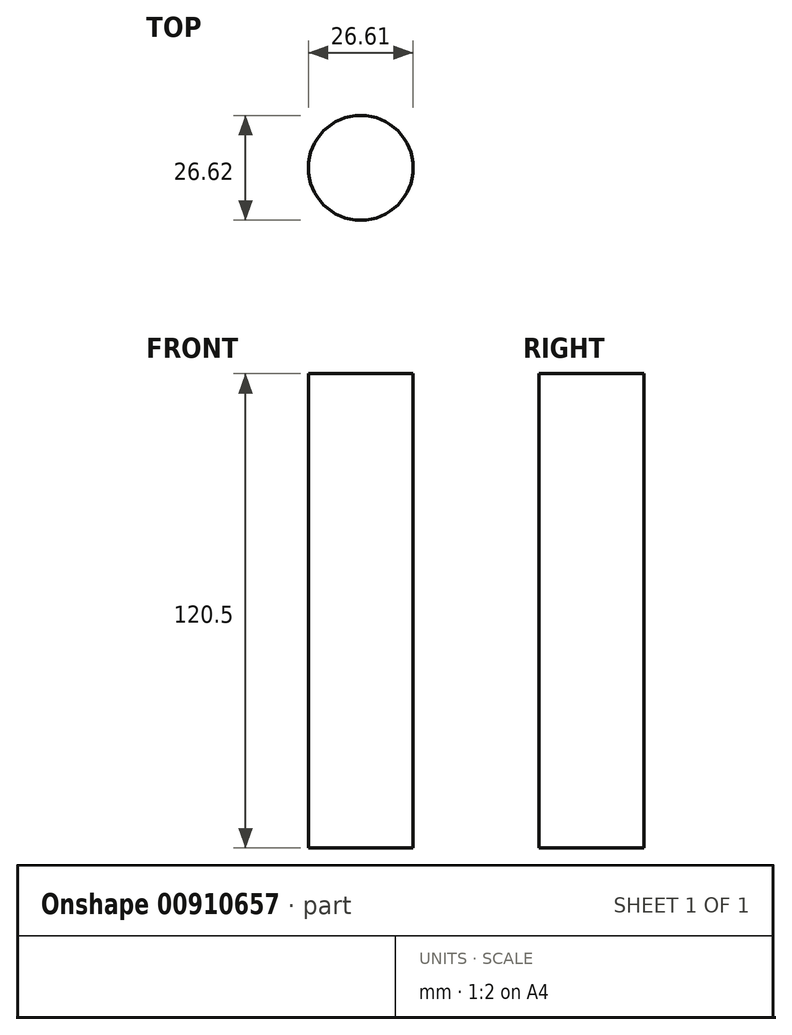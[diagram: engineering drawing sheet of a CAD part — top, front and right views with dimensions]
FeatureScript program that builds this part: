
annotation { "Feature Type Name" : "Feature", "Feature Type Description" : "" }
export const myFeature = defineFeature(function(context is Context, id is Id, definition is map)
    precondition{}
    {
        {
            var Q0;
            Q0=qCreatedBy(makeId("Top.planeOp"),FACE);
            var sketch = newSketch(context, id + "F0", { "sketchPlane" : qUnion([Q0])});
            skCircle(sketch, "E0", {"center": v(-49.8, 22.43) * mm, "radius": 13.3 * mm});
            skSolve(sketch);
        }
        {
            var Q0;
            Q0=makeQuery(id+"F0.imprint","IMPRINT",FACE,{"disambiguationData":[TD([[makeQuery(id+"F0.imprint","IMPRINT",EDGE,{"derivedFrom":sQuery(id+"F0.wireOp",EDGE,"E0")}),1.0]])]});
            extrude(context, id + "F1", {"entities" : qUnion([Q0]), "depth" : 120.5 * mm, "offsetDistance" : 25 * mm});
        }
    });
